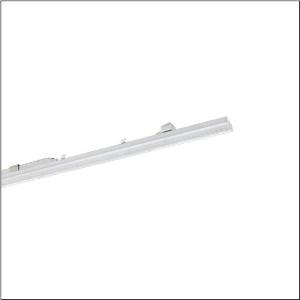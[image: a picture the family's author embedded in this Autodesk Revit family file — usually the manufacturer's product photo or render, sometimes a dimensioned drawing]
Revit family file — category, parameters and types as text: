
# Revit family: tl_l_5wd7a8h0h2b5
name_source: partatom
category: Lighting Fixtures
units: mm (PartAtom-declared; Revit-internal decimal feet)

## family parameters
Cut with Voids When Loaded = No
Host = Face
Light Source = No
Part Type = Normal
Room Calculation Point = No
Round Connector Dimension = Use Diameter
Shared = No

## types (1)
- --- (1 x LED, 850 lm, 4.5 W, 4000K)
    Apparent Load = 5 VA
    CIE Flux Codes = 49 84 98 100 100
    Color Rendering = 80
    Color Temperature = 4000K
    Default Elevation = 1800 mm
    Description = TL L, luminaire insert, of sheet steel, galvanised, coil coated, white, length: 1.500mm, width: 66mm, height: 67mm, surge protection,LED rated luminous flux: 4.990lm, light colour: 840, control gear: emergency light, with terminal, 3-pole, mains connection: 230..240V, AC, 50/60Hz, rated input power: 34W, micro fuse,primary optical cover: cover, of PMMA, light emission: direct distribution, protection rating (complete): as luminaire, insulation class (complete): insulation class I (protective earthing), certification: CE, impact resistance: IK06, permissible ambient temperature for indoor applications: +5..+35°C, packaging unit: 1 piece
    Height = 120 mm
    Lamp = 1 x LED
    Lamp Light Flux = 850 lm
    Lamp Power = 4.5 W
    Lamp count = 1
    Length = 1690 mm
    Luminous efficacy = 189 lm/W
    Manufacturer = Siteco
    ModVariant = No
    Model = 5WD7A8H0H2B5
    Mounting Place = Ceiling
    Mounting Type = Pendant
    Number of Poles = 1
    OnlyDefault = Yes
    Power Factor = 1
    Product Name = TL L
    Product group = luminaire insert
    ProductGroupID = 901
    Protection Class = Protection class I
    Protection Degree = Degree of protection
    RLX_Detail_Level = 1
    RLX_Emergency_Light_Flux = 0 lm
    RLX_Emergency_Type = 0
    RLX_Emergency_Type_DB = No
    RlxData = <blob elided: 17397 chars, md5=530ca558>
    Socket = socket
    Standby Power = 0 W
    System Light Flux = 850 lm
    System Power = 5 W
    Type Comments = : emergency light operation: 3 h
    Type Image = l_1294382.jpg
    URL = http://relux.com
    VarID = @adj_030877
    Voltage = 0 V
    Weight = 0.00 kg
    Width = 208 mm

## geometry (parser evidence)
native form markers: Blend x4, Sweep x12
no freeform markers — native parametric forms only
